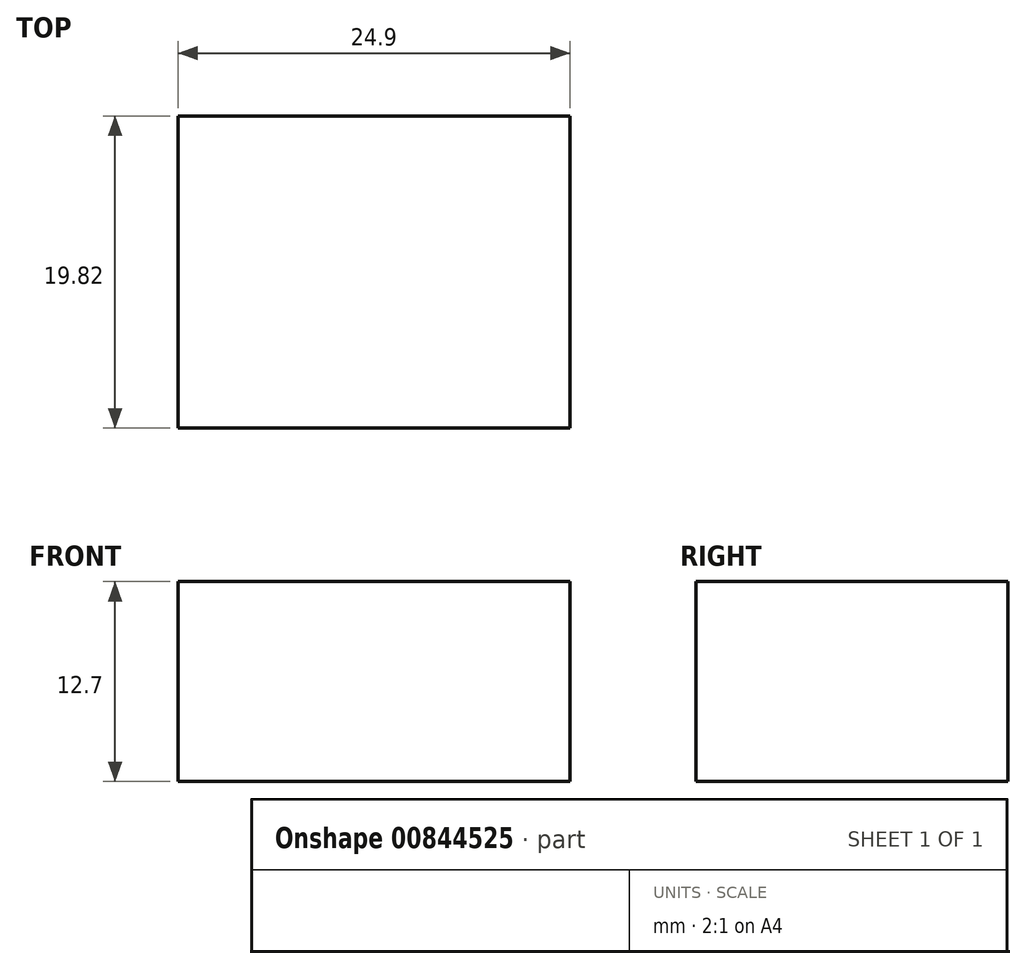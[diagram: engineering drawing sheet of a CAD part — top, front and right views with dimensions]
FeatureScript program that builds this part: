
annotation { "Feature Type Name" : "Feature", "Feature Type Description" : "" }
export const myFeature = defineFeature(function(context is Context, id is Id, definition is map)
    precondition{}
    {
        {
            var Q0;
            Q0=qCreatedBy(makeId("Top.planeOp"),FACE);
            var sketch = newSketch(context, id + "F0", { "sketchPlane" : qUnion([Q0])});
            skPoint(sketch, "E0.middle", {"position": v(0, 0) * mm});
            skCircle(sketch, "E1", {"center": v(-6.35, 0) * mm, "radius": 2.16 * mm, "construction": true});
            skCircle(sketch, "E2", {"center": v(6.35, 0) * mm, "radius": 2.16 * mm, "construction": true});
            skLineSegment(sketch, "E3.bottom", {"start": v(-12.45, 9.9) * mm, "end": v(12.45, 9.9) * mm});
            skLineSegment(sketch, "E3.top", {"start": v(-12.45, -9.9) * mm, "end": v(12.45, -9.9) * mm});
            skLineSegment(sketch, "E3.left", {"start": v(-12.45, 9.9) * mm, "end": v(-12.45, -9.9) * mm});
            skLineSegment(sketch, "E3.right", {"start": v(12.45, 9.9) * mm, "end": v(12.45, -9.9) * mm});
            skSolve(sketch);
        }
        {
            var Q0;
            Q0=makeQuery(id+"F0.imprint","IMPRINT",FACE,{"disambiguationData":[TD([[makeQuery(id+"F0.imprint","IMPRINT",EDGE,{"derivedFrom":sQuery(id+"F0.wireOp",EDGE,"E3.bottom")}),-1.0]])]});
            extrude(context, id + "F1", {"entities" : qUnion([Q0]), "endBound" : BoundingType.SYMMETRIC, "depth" : 12.7 * mm, "offsetDistance" : 25.4 * mm});
        }
    });
